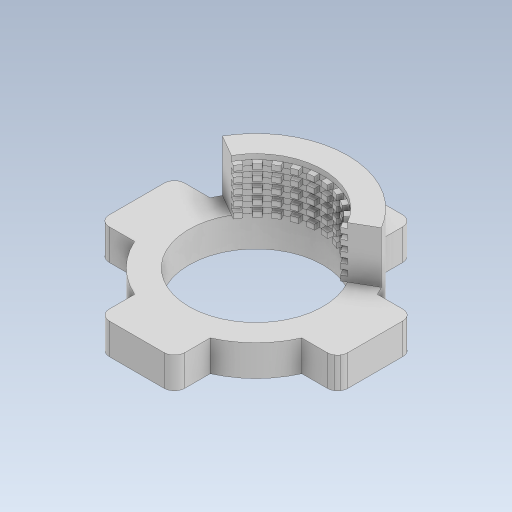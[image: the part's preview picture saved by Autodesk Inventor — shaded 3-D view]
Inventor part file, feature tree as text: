
AUTODESK INVENTOR PART (.ipt)
format: ipt  version: 2023 (Build 270158000, 158)  size: 557,056 bytes
history: native  units: in
note: dims shown in document units (in); Inventor stores cm internally (conversion verified against a paired STEP export)
features: sketch x15, extrude x11, projected_geometry x5, plane x4, revolve x2
ambient origin geometry x8: Origin, YZ Plane, XZ Plane, XY Plane, X Axis, Y Axis, Z Axis, Center Point
bodies: Solid1 (feature_tree)
feature tree (37):
  extrude  "Extrusion1"  Depth=0.2362in TaperAngle=0.0deg
  extrude  "Extrusion2"  Depth=0.3937in TaperAngle=0.0deg
  extrude  "Extrusion3"  Depth=0.0394in TaperAngle=120.0deg
  revolve  "Revolution1"  [1 undecoded]
  extrude  "Extrusion4"  Depth=0.1969in TaperAngle=0.0deg
  extrude  "Extrusion5"  Depth=0.2362in
  extrude  "Extrusion6"  Depth=0.0787in
  plane  "Work Plane1"
  sketch  "Sketch10"  dims[d31=0.3937in d32=0.0in d40=0.4724in]
  plane  "Work Plane2"
  sketch  "Sketch13"  dims[d41=0.0787in d42=0.3937in]
  plane  "Work Plane3"
  sketch  "Sketch14"  dims[d45=0.315in d46=0.3937in]
  plane  "Work Plane4"
  extrude  "Extrusion8"  Depth=0.4724in
  sketch  "Sketch19"  dims[d87=45.0deg d88=0.0in d89=0.0in]
  extrude  "Extrusion9"  Depth=0.3937in
  extrude  "Extrusion10"  Depth=0.3937in
  extrude  "Extrusion11"  Depth=0.3937in
  revolve  "Revolution2"  [1 undecoded]
  extrude  "Extrusion12"  Depth=0.315in TaperAngle=0.0deg
  sketch  "Sketch1"  dims[d0=1.0236in d1=0.2362in d2=0.0in]
  sketch  "Sketch2"  dims[d3=120.0deg d4=0.3937in d5=0.0in]
  sketch  "Sketch3"  dims[d6=0.0394in d7=7.874in d9=120.0deg]
  sketch  "Sketch4"  dims[d11=0.3937in d12=0.0in d14=3.937in d16=0.0394in d17=0.3937in d19=0.3937in]
  sketch  "Sketch5"  dims[d21=360.0deg d22=1.9685in d23=0.1969in d24=0.0in d25=0.0in]
  sketch  "Sketch6"  dims[d26=0.2362in d27=1.2511in]
  sketch  "Sketch7"  dims[d28=1.3998in d29=0.0787in d30=0.0687in]
  sketch  "Sketch18"  dims[d53=0.0394in d54=0.3937in]
  projected_geometry  "Projected Loop4"
  projected_geometry  "Projected Loop5"
  sketch  "Sketch20"  dims[d91=0.3937in d92=0.0in d93=0.315in d94=0.0in]
  projected_geometry  "Projected Loop6"
  sketch  "Sketch23"  dims[d95=0.315in d96=0.0in]
  projected_geometry  "Projected Loop7"
  sketch  "Sketch24"  dims[d102=90.0deg d103=0.3937in d104=-0.0687in]
  projected_geometry  "Projected Loop8"
note: 2 required parameter values undecoded (feature->parameter linkage not recoverable at this tier; creation-order binding heuristic only, values carry confidence <= 0.55)
